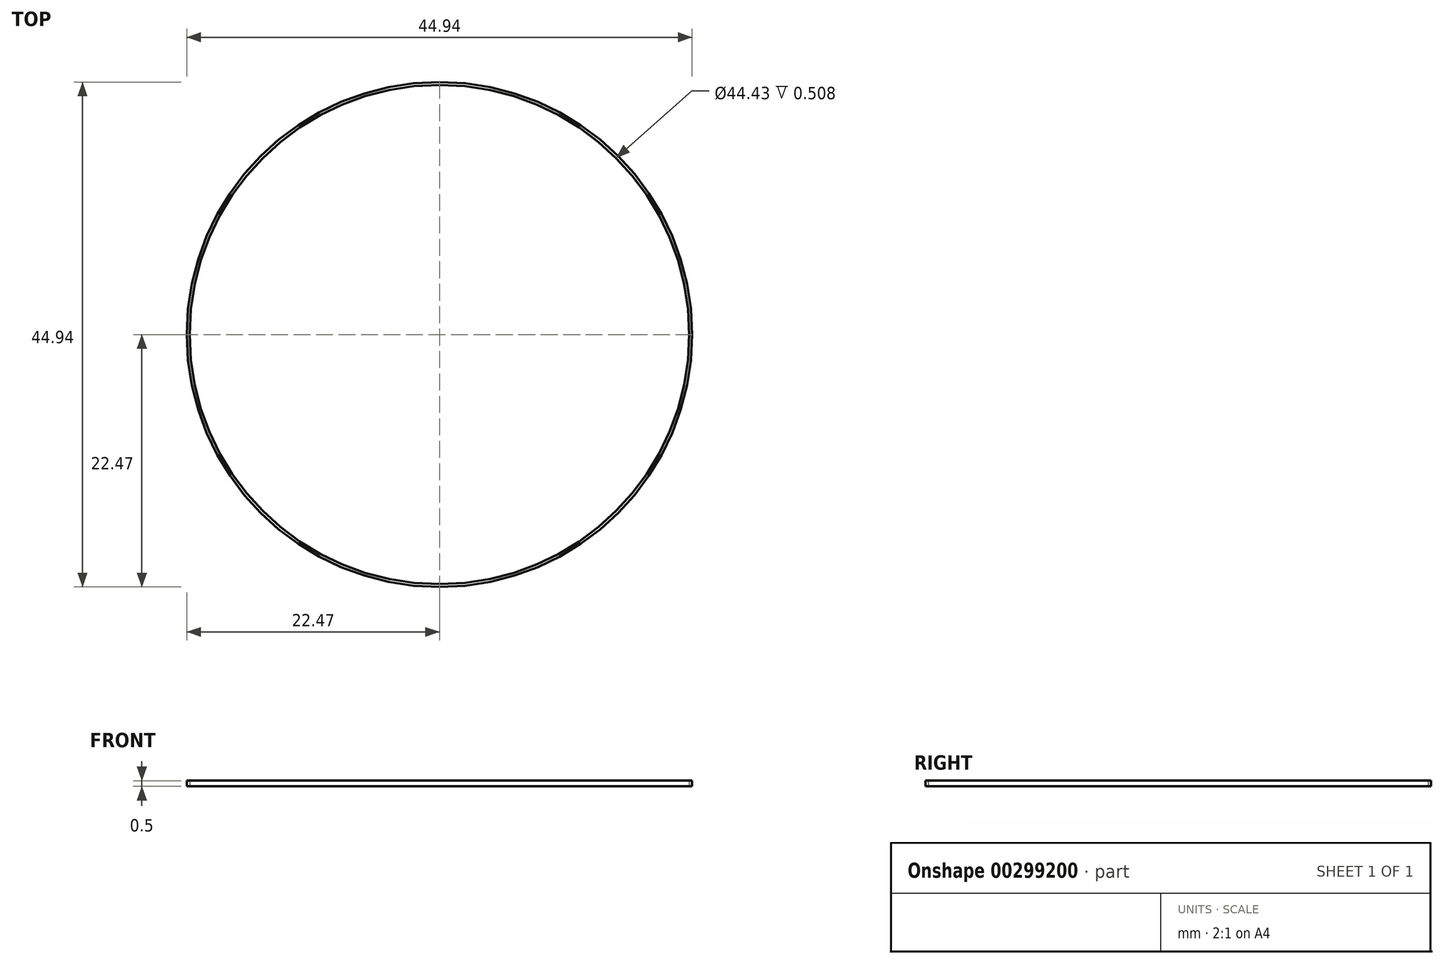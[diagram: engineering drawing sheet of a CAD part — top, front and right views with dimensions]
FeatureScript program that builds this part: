
annotation { "Feature Type Name" : "Feature", "Feature Type Description" : "" }
export const myFeature = defineFeature(function(context is Context, id is Id, definition is map)
    precondition{}
    {
        {
            var Q0;
            Q0=qCreatedBy(makeId("Top.planeOp"),FACE);
            var sketch = newSketch(context, id + "F0", { "sketchPlane" : qUnion([Q0])});
            skCircle(sketch, "E0", {"center": v(0, 0) * mm, "radius": 22.22 * mm});
            skLineSegment(sketch, "E1", {"start": v(0, 22.22) * mm, "end": v(0, -22.22) * mm});
            skLineSegment(sketch, "E2.0", {"start": v(-1.27, 22.18) * mm, "end": v(-1.27, -22.18) * mm});
            skLineSegment(sketch, "E3.0", {"start": v(-2.54, 22.07) * mm, "end": v(-2.54, -22.07) * mm});
            skLineSegment(sketch, "E4.0", {"start": v(-3.81, 21.89) * mm, "end": v(-3.81, -21.89) * mm});
            skLineSegment(sketch, "E5.0", {"start": v(-5.08, 21.63) * mm, "end": v(-5.08, -21.63) * mm});
            skLineSegment(sketch, "E6.0", {"start": v(-6.35, 21.29) * mm, "end": v(-6.35, -21.29) * mm});
            skLineSegment(sketch, "E7.0", {"start": v(-7.62, 20.87) * mm, "end": v(-7.62, -20.87) * mm});
            skLineSegment(sketch, "E8.0", {"start": v(-10.16, 19.76) * mm, "end": v(-10.16, -19.76) * mm});
            skLineSegment(sketch, "E9.0", {"start": v(-11.43, 19.05) * mm, "end": v(-11.43, -19.05) * mm});
            skLineSegment(sketch, "E10.0", {"start": v(-12.7, 18.23) * mm, "end": v(-12.7, -18.23) * mm});
            skLineSegment(sketch, "E11.0", {"start": v(-13.97, 17.27) * mm, "end": v(-13.97, -17.27) * mm});
            skLineSegment(sketch, "E12.0", {"start": v(-15.24, 16.16) * mm, "end": v(-15.24, -16.16) * mm});
            skLineSegment(sketch, "E13.0", {"start": v(-16.51, 14.87) * mm, "end": v(-16.51, -14.87) * mm});
            skLineSegment(sketch, "E14.0", {"start": v(-17.78, 13.32) * mm, "end": v(-17.78, -13.32) * mm});
            skLineSegment(sketch, "E15.0", {"start": v(-19.05, 11.43) * mm, "end": v(-19.05, -11.43) * mm});
            skLineSegment(sketch, "E16.0", {"start": v(-20.32, 8.98) * mm, "end": v(-20.32, -8.98) * mm});
            skLineSegment(sketch, "E17.0", {"start": v(-21.6, 5.24) * mm, "end": v(-21.6, -5.24) * mm});
            skLineSegment(sketch, "E18.0", {"start": v(-8.9, 20.36) * mm, "end": v(-8.9, -20.36) * mm});
            skLineSegment(sketch, "E19.MirrorCS", {"start": v(1.27, 22.18) * mm, "end": v(1.27, -22.18) * mm});
            skLineSegment(sketch, "E20.MirrorCS", {"start": v(2.54, 22.07) * mm, "end": v(2.54, -22.07) * mm});
            skLineSegment(sketch, "E21.MirrorCS", {"start": v(3.81, 21.89) * mm, "end": v(3.81, -21.89) * mm});
            skLineSegment(sketch, "E22.MirrorCS", {"start": v(6.35, 21.29) * mm, "end": v(6.35, -21.29) * mm});
            skLineSegment(sketch, "E23.MirrorCS", {"start": v(5.08, 21.63) * mm, "end": v(5.08, -21.63) * mm});
            skLineSegment(sketch, "E24.MirrorCS", {"start": v(11.43, 19.05) * mm, "end": v(11.43, -19.05) * mm});
            skLineSegment(sketch, "E25.MirrorCS", {"start": v(12.7, 18.23) * mm, "end": v(12.7, -18.23) * mm});
            skLineSegment(sketch, "E26.MirrorCS", {"start": v(10.16, 19.76) * mm, "end": v(10.16, -19.76) * mm});
            skLineSegment(sketch, "E27.MirrorCS", {"start": v(7.62, 20.87) * mm, "end": v(7.62, -20.87) * mm});
            skLineSegment(sketch, "E28.MirrorCS", {"start": v(8.9, 20.36) * mm, "end": v(8.9, -20.36) * mm});
            skLineSegment(sketch, "E29.MirrorCS", {"start": v(13.97, 17.27) * mm, "end": v(13.97, -17.27) * mm});
            skLineSegment(sketch, "E30.MirrorCS", {"start": v(15.24, 16.16) * mm, "end": v(15.24, -16.16) * mm});
            skLineSegment(sketch, "E31.MirrorCS", {"start": v(16.51, 14.87) * mm, "end": v(16.51, -14.87) * mm});
            skLineSegment(sketch, "E32.MirrorCS", {"start": v(17.78, 13.32) * mm, "end": v(17.78, -13.32) * mm});
            skLineSegment(sketch, "E33.MirrorCS", {"start": v(19.05, 11.43) * mm, "end": v(19.05, -11.43) * mm});
            skLineSegment(sketch, "E34.MirrorCS", {"start": v(20.32, 8.98) * mm, "end": v(20.32, -8.98) * mm});
            skLineSegment(sketch, "E35.MirrorCS", {"start": v(21.6, 5.24) * mm, "end": v(21.6, -5.24) * mm});
            skCircle(sketch, "E36.0", {"center": v(0, 0) * mm, "radius": 22.47 * mm});
            skSolve(sketch);
        }
        {
            var Q0;
            Q0=makeQuery(id+"F0.imprint","IMPRINT",FACE,{"disambiguationData":[TD([[makeQuery(id+"F0.imprint","IMPRINT",EDGE,{"derivedFrom":sQuery(id+"F0.wireOp",EDGE,"E36.0")}),1.0]])]});
            extrude(context, id + "F1", {"entities" : qUnion([Q0]), "depth" : 0.5 * mm, "symmetric" : true});
        }
        {
            var Q0;
            Q0=sQuery(id+"F0.wireOp",EDGE,"E34.MirrorCS");
            var Q1;
            Q1=sQuery(id+"F0.wireOp",EDGE,"E7.0");
            var Q2;
            Q2=sQuery(id+"F0.wireOp",EDGE,"E18.0");
            var Q3;
            Q3=sQuery(id+"F0.wireOp",EDGE,"E11.0");
            var Q4;
            Q4=sQuery(id+"F0.wireOp",EDGE,"E10.0");
            var Q5;
            Q5=sQuery(id+"F0.wireOp",EDGE,"E35.MirrorCS");
            var Q6;
            Q6=sQuery(id+"F0.wireOp",EDGE,"E26.MirrorCS");
            var Q7;
            Q7=sQuery(id+"F0.wireOp",EDGE,"E22.MirrorCS");
            var Q8;
            Q8=sQuery(id+"F0.wireOp",EDGE,"E28.MirrorCS");
            var Q9;
            Q9=sQuery(id+"F0.wireOp",EDGE,"E17.0");
            var Q10;
            Q10=sQuery(id+"F0.wireOp",EDGE,"E16.0");
            var Q11;
            Q11=sQuery(id+"F0.wireOp",EDGE,"E4.0");
            var Q12;
            Q12=sQuery(id+"F0.wireOp",EDGE,"E20.MirrorCS");
            var Q13;
            Q13=sQuery(id+"F0.wireOp",EDGE,"E13.0");
            var Q14;
            Q14=sQuery(id+"F0.wireOp",EDGE,"E32.MirrorCS");
            var Q15;
            Q15=sQuery(id+"F0.wireOp",EDGE,"E14.0");
            var Q16;
            Q16=sQuery(id+"F0.wireOp",EDGE,"E29.MirrorCS");
            var Q17;
            Q17=sQuery(id+"F0.wireOp",EDGE,"E23.MirrorCS");
            var Q18;
            Q18=sQuery(id+"F0.wireOp",EDGE,"E9.0");
            var Q19;
            Q19=sQuery(id+"F0.wireOp",EDGE,"E25.MirrorCS");
            var Q20;
            Q20=sQuery(id+"F0.wireOp",EDGE,"E12.0");
            var Q21;
            Q21=sQuery(id+"F0.wireOp",EDGE,"E24.MirrorCS");
            var Q22;
            Q22=sQuery(id+"F0.wireOp",EDGE,"E27.MirrorCS");
            var Q23;
            Q23=sQuery(id+"F0.wireOp",EDGE,"E1");
            var Q24;
            Q24=sQuery(id+"F0.wireOp",EDGE,"E2.0");
            var Q25;
            Q25=sQuery(id+"F0.wireOp",EDGE,"E3.0");
            var Q26;
            Q26=sQuery(id+"F0.wireOp",EDGE,"E5.0");
            var Q27;
            Q27=sQuery(id+"F0.wireOp",EDGE,"E6.0");
            var Q28;
            Q28=sQuery(id+"F0.wireOp",EDGE,"E8.0");
            var Q29;
            Q29=sQuery(id+"F0.wireOp",EDGE,"E21.MirrorCS");
            var Q30;
            Q30=sQuery(id+"F0.wireOp",EDGE,"E30.MirrorCS");
            var Q31;
            Q31=sQuery(id+"F0.wireOp",EDGE,"E19.MirrorCS");
            var Q32;
            Q32=sQuery(id+"F0.wireOp",EDGE,"E33.MirrorCS");
            var Q33;
            Q33=sQuery(id+"F0.wireOp",EDGE,"E15.0");
            var Q34;
            Q34=sQuery(id+"F0.wireOp",EDGE,"E31.MirrorCS");
            extrude(context, id + "F2", {"bodyType" : ToolBodyType.SURFACE, "surfaceEntities" : qUnion([Q0, Q1, Q2, Q3, Q4, Q5, Q6, Q7, Q8, Q9, Q10, Q11, Q12, Q13, Q14, Q15, Q16, Q17, Q18, Q19, Q20, Q21, Q22, Q23, Q24, Q25, Q26, Q27, Q28, Q29, Q30, Q31, Q32, Q33, Q34]), "depth" : 0.05 * mm, "symmetric" : true});
        }
    });
